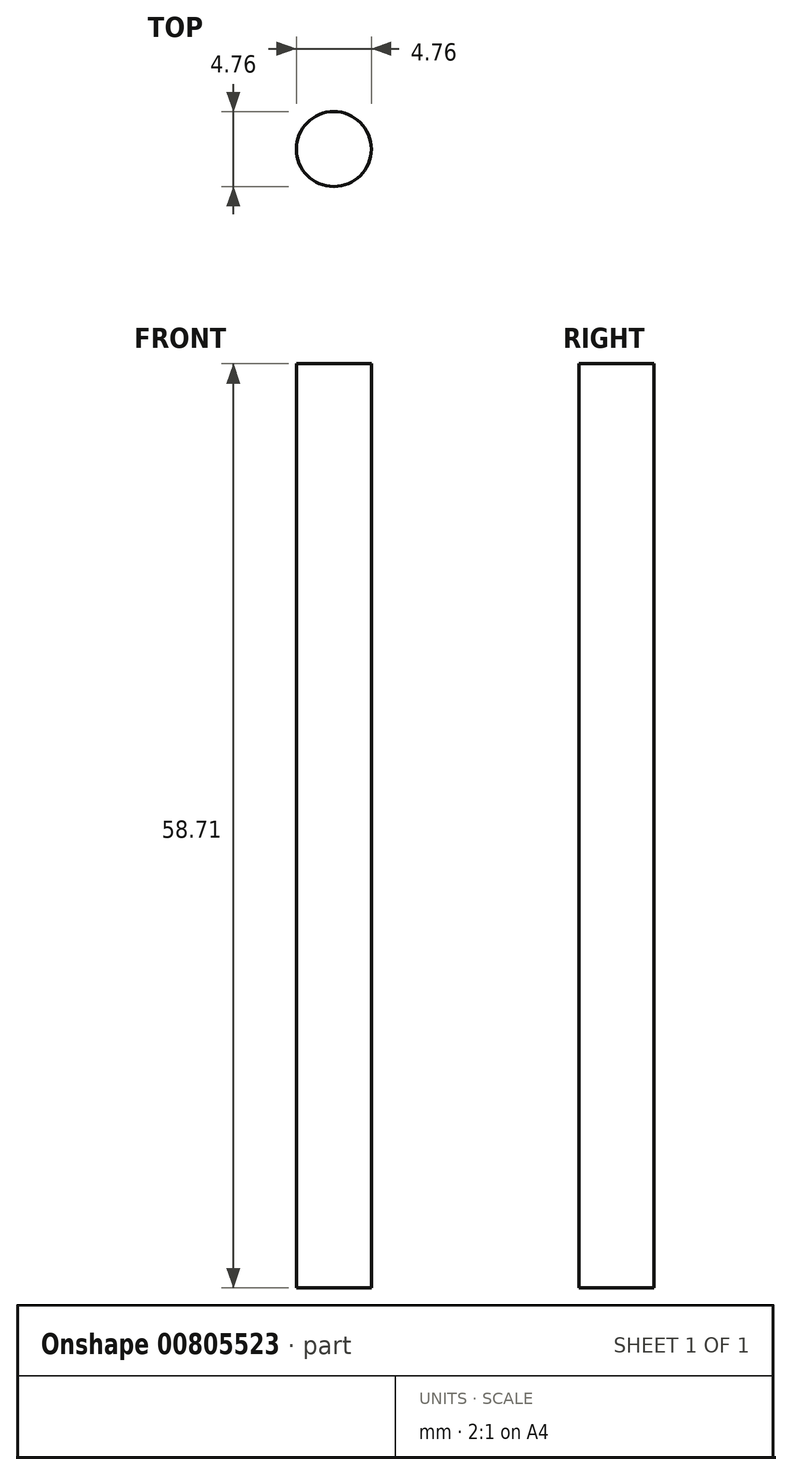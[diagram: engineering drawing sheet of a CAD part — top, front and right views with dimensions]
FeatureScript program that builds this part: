
annotation { "Feature Type Name" : "Feature", "Feature Type Description" : "" }
export const myFeature = defineFeature(function(context is Context, id is Id, definition is map)
    precondition{}
    {
        {
            var Q0;
            Q0=qCreatedBy(makeId("Top.planeOp"),FACE);
            var sketch = newSketch(context, id + "F0", { "sketchPlane" : qUnion([Q0])});
            skCircle(sketch, "E0", {"center": v(0, 0) * mm, "radius": 2.38 * mm});
            skSolve(sketch);
        }
        {
            var Q0;
            Q0=makeQuery(id+"F0.imprint","IMPRINT",FACE,{"disambiguationData":[TD([[makeQuery(id+"F0.imprint","IMPRINT",EDGE,{"derivedFrom":sQuery(id+"F0.wireOp",EDGE,"E0")}),1.0]])]});
            extrude(context, id + "F1", {"entities" : qUnion([Q0]), "depth" : 58.7 * mm, "offsetDistance" : 25 * mm});
        }
    });
